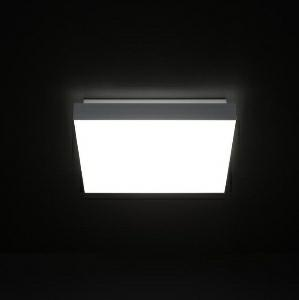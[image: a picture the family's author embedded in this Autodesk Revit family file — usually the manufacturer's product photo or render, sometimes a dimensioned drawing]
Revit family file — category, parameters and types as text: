
# Revit family: spectral_norea_norea-qa_625_5200_840_mps_75bb
name_source: partatom
category: Lighting Fixtures
revit_build: Autodesk Revit 2016 (Build: 20150220_1215(x64)
units: mm (PartAtom-declared; Revit-internal decimal feet)

## family parameters
Cut with Voids When Loaded = No
Host = Face
Light Source = No
Part Type = Normal
Room Calculation Point = No
Round Connector Dimension = Use Diameter
Shared = No

## types (1)
- SPECTRAL NOREA (1 x )
    Apparent Load = 0 VA
    Approval mark = CE
    CIE Flux Codes = 64 90 97 96 69
    Control Gear = Electronic transformer
    Default Elevation = 1800 mm
    Description = SPT0000105
NOREA surface-mounted luminaire

Design:
Square luminaire element with a microprism panel in a natural anodised aluminium profile frame surround. The frame is suspended at the metal body. The LED module is formed as a square LED flat board and screwed to the luminaire element. For connection of the luminaire this can be hinged down and fastened with screws at an oblong hole in the powder-coated metal body. The indirect component is ensured by recesses in the top of the metal body. The metal body accommodates the electrical components and electronic ballast. Luminaire with heat-resistant wiring. Variant suitable for office use with a microprism panel MPS. The LED points are visible as circles on the microprism panel. Suitable for ceiling or wall mounting. Also in a dimmable version. Light colours 830 und 840. Protection rating IP20, safety class I.

Colour:
Housing – similar to RAL 9016 White silk matt;
Frame – natural anodised
    Height = 95 mm
    Lamp = 1 x
    Lamp count = 1
    Length = 625 mm
    Luminous efficacy = 0 lm/W
    Manufacturer = Ridi
    ModVariant = No
    Model = NOREA-QA 625/5200/840 MPS
    Mounting Place = Ceiling
    Mounting Type = Surface mounted
    Number of Poles = 1
    OnlyDefault = Yes
    Power Factor = 1
    Product Name = SPECTRAL NOREA
    Product group = Ceiling mounted luminaire
    ProductGroupID = 3
    Protection Class = Protection class
    Protection Degree = IP 20
    RlxData = <blob elided: 28813 chars, md5=ce26a311>
    Socket = socket
    Standby Power = 0 W
    System Light Flux = 0 lm
    System Power = 0 W
    Type Image = noreaquad05_-_kopie.jpg
    URL = http://reluxnet.relux.com
    VarID = 1
    Voltage = 0 V
    Weight = 0.00 kg
    Width = 625 mm

## geometry (parser evidence)
native form markers: Blend x4, Sweep x8
no freeform markers — native parametric forms only
